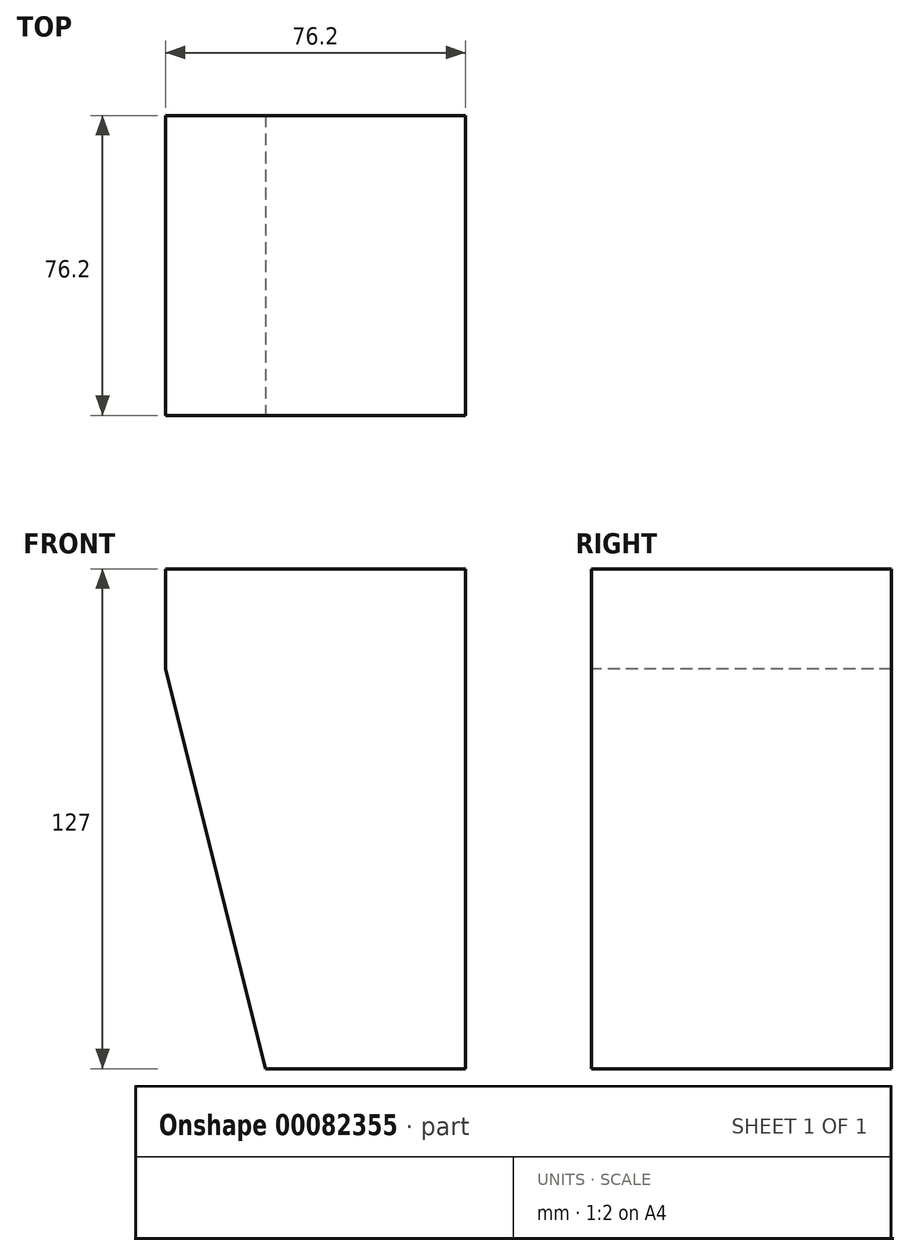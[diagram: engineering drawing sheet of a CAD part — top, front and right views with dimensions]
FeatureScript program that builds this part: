
annotation { "Feature Type Name" : "Feature", "Feature Type Description" : "" }
export const myFeature = defineFeature(function(context is Context, id is Id, definition is map)
    precondition{}
    {
        {
            var Q0;
            Q0=qCreatedBy(makeId("Front.planeOp"),FACE);
            var sketch = newSketch(context, id + "F0", { "sketchPlane" : qUnion([Q0])});
            skLineSegment(sketch, "E0.bottom", {"start": v(38.1, -63.5) * mm, "end": v(-38.1, -63.5) * mm});
            skLineSegment(sketch, "E0.top", {"start": v(38.1, 63.5) * mm, "end": v(-38.1, 63.5) * mm});
            skLineSegment(sketch, "E0.left", {"start": v(38.1, -63.5) * mm, "end": v(38.1, 63.5) * mm});
            skLineSegment(sketch, "E0.right", {"start": v(-38.1, -63.5) * mm, "end": v(-38.1, 63.5) * mm});
            skPoint(sketch, "E0.middle", {"position": v(0, 0) * mm});
            skSolve(sketch);
        }
        {
            var Q0;
            Q0 = qSketchRegion(id + "F0", true);
            extrude(context, id + "F1", {"entities" : qUnion([Q0]), "depth" : 76.2 * mm, "symmetric" : true});
        }
        {
            var Q0;
            Q0=makeQuery(id+"F1.opExtrude","CAP_FACE",FACE,{"disambiguationData":[OSD([sQuery(id+"F0.wireOp",EDGE,"E0.bottom"),sQuery(id+"F0.wireOp",EDGE,"E0.top"),sQuery(id+"F0.wireOp",EDGE,"E0.left"),sQuery(id+"F0.wireOp",EDGE,"E0.right")])],"isStart":false});
            var sketch = newSketch(context, id + "F2", { "sketchPlane" : qUnion([Q0])});
            skLineSegment(sketch, "E1", {"start": v(-38.1, -63.5) * mm, "end": v(-38.1, 38.1) * mm});
            skLineSegment(sketch, "E2", {"start": v(-38.1, 38.1) * mm, "end": v(-12.7, -63.5) * mm});
            skLineSegment(sketch, "E3", {"start": v(-12.7, -63.5) * mm, "end": v(-38.1, -63.5) * mm});
            skSolve(sketch);
        }
        {
            var Q0;
            Q0 = qSketchRegion(id + "F2", true);
            extrude(context, id + "F3", {"entities" : qUnion([Q0]), "operationType" : NewBodyOperationType.REMOVE, "endBound" : BoundingType.THROUGH_ALL, "oppositeDirection" : true, "depth" : 25.4 * mm});
        }
    });
